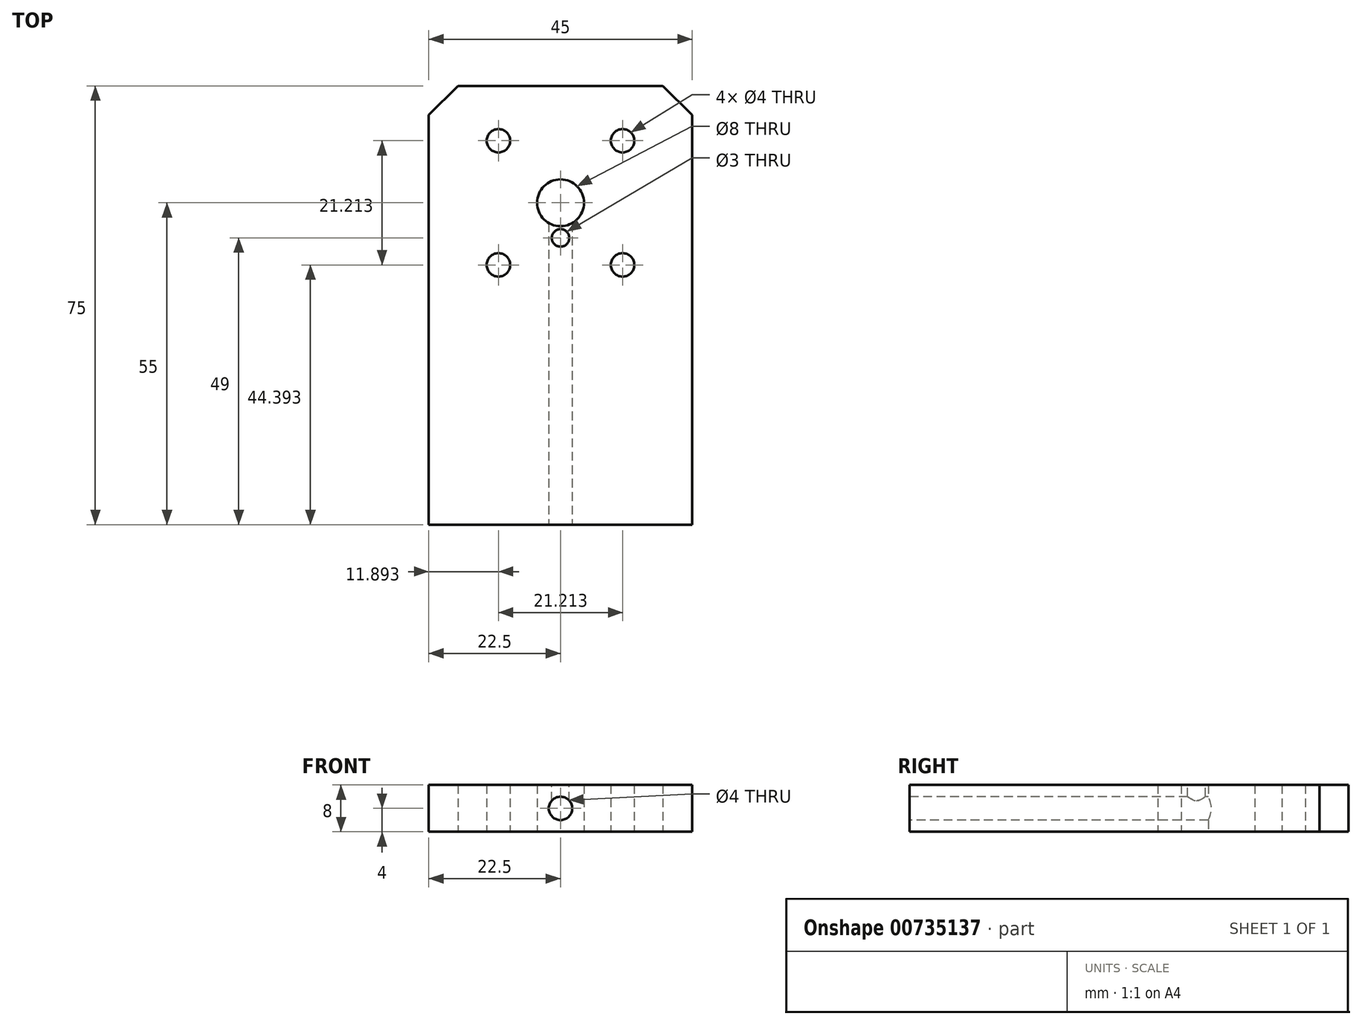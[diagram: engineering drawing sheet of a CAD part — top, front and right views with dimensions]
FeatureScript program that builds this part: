
annotation { "Feature Type Name" : "Feature", "Feature Type Description" : "" }
export const myFeature = defineFeature(function(context is Context, id is Id, definition is map)
    precondition{}
    {
        {
            var Q0;
            Q0=qCreatedBy(makeId("Top.planeOp"),FACE);
            var sketch = newSketch(context, id + "F0", { "sketchPlane" : qUnion([Q0])});
            skLineSegment(sketch, "E0", {"start": v(0, 0) * mm, "end": v(0, 70) * mm});
            skLineSegment(sketch, "E1", {"start": v(5, 75) * mm, "end": v(40, 75) * mm});
            skLineSegment(sketch, "E2", {"start": v(45, 70) * mm, "end": v(45, 0) * mm});
            skLineSegment(sketch, "E3", {"start": v(45, 0) * mm, "end": v(0, 0) * mm});
            skLineSegment(sketch, "E4", {"start": v(0, 70) * mm, "end": v(5, 75) * mm});
            skLineSegment(sketch, "E5", {"start": v(40, 75) * mm, "end": v(45, 70) * mm});
            skLineSegment(sketch, "E6", {"start": v(0, 55) * mm, "end": v(45, 55) * mm, "construction": true});
            skCircle(sketch, "E7", {"center": v(22.5, 55) * mm, "radius": 4 * mm});
            skCircle(sketch, "E8", {"center": v(22.5, 55) * mm, "radius": 15 * mm, "construction": true});
            skCircle(sketch, "E9", {"center": v(33.1, 65.6) * mm, "radius": 2 * mm});
            skCircle(sketch, "E10.1.0", {"center": v(11.9, 65.6) * mm, "radius": 2 * mm});
            skCircle(sketch, "E10.2.0", {"center": v(11.9, 44.4) * mm, "radius": 2 * mm});
            skCircle(sketch, "E10.3.0", {"center": v(33.1, 44.4) * mm, "radius": 2 * mm});
            skSolve(sketch);
        }
        {
            var Q0;
            Q0 = qSketchRegion(id + "F0", true);
            extrude(context, id + "F1", {"entities" : qUnion([Q0]), "depth" : 8 * mm, "offsetDistance" : 25 * mm});
        }
        {
            var Q0;
            Q0=makeQuery(id+"F1.opExtrude","SWEPT_FACE",FACE,{"disambiguationData":[OSD([sQuery(id+"F0.wireOp",EDGE,"E3")])]});
            var sketch = newSketch(context, id + "F2", { "sketchPlane" : qUnion([Q0])});
            skLineSegment(sketch, "E11", {"start": v(45, 4) * mm, "end": v(0, 4) * mm, "construction": true});
            skCircle(sketch, "E12", {"center": v(22.5, 4) * mm, "radius": 2 * mm});
            skSolve(sketch);
        }
        {
            var Q0;
            Q0 = qSketchRegion(id + "F2", true);
            extrude(context, id + "F3", {"entities" : qUnion([Q0]), "operationType" : NewBodyOperationType.REMOVE, "oppositeDirection" : true, "depth" : 53 * mm, "offsetDistance" : 25 * mm});
        }
        {
            var Q0;
            Q0=makeQuery(id+"F1.opExtrude","CAP_FACE",FACE,{"disambiguationData":[OSD([sQuery(id+"F0.wireOp",EDGE,"E0"),sQuery(id+"F0.wireOp",EDGE,"E1"),sQuery(id+"F0.wireOp",EDGE,"E2"),sQuery(id+"F0.wireOp",EDGE,"E3"),sQuery(id+"F0.wireOp",EDGE,"E4"),sQuery(id+"F0.wireOp",EDGE,"E5"),sQuery(id+"F0.wireOp",EDGE,"E7"),sQuery(id+"F0.wireOp",EDGE,"E9"),sQuery(id+"F0.wireOp",EDGE,"E10.1.0"),sQuery(id+"F0.wireOp",EDGE,"E10.2.0"),sQuery(id+"F0.wireOp",EDGE,"E10.3.0")])],"isStart":false});
            var sketch = newSketch(context, id + "F4", { "sketchPlane" : qUnion([Q0])});
            skLineSegment(sketch, "E13", {"start": v(22.5, 0) * mm, "end": v(22.5, 55) * mm, "construction": true});
            skCircle(sketch, "E14", {"center": v(22.5, 49) * mm, "radius": 1.5 * mm});
            skSolve(sketch);
        }
        {
            var Q0;
            Q0 = qSketchRegion(id + "F4", true);
            extrude(context, id + "F5", {"entities" : qUnion([Q0]), "operationType" : NewBodyOperationType.REMOVE, "oppositeDirection" : true, "depth" : 3 * mm, "offsetDistance" : 25 * mm});
        }
    });
